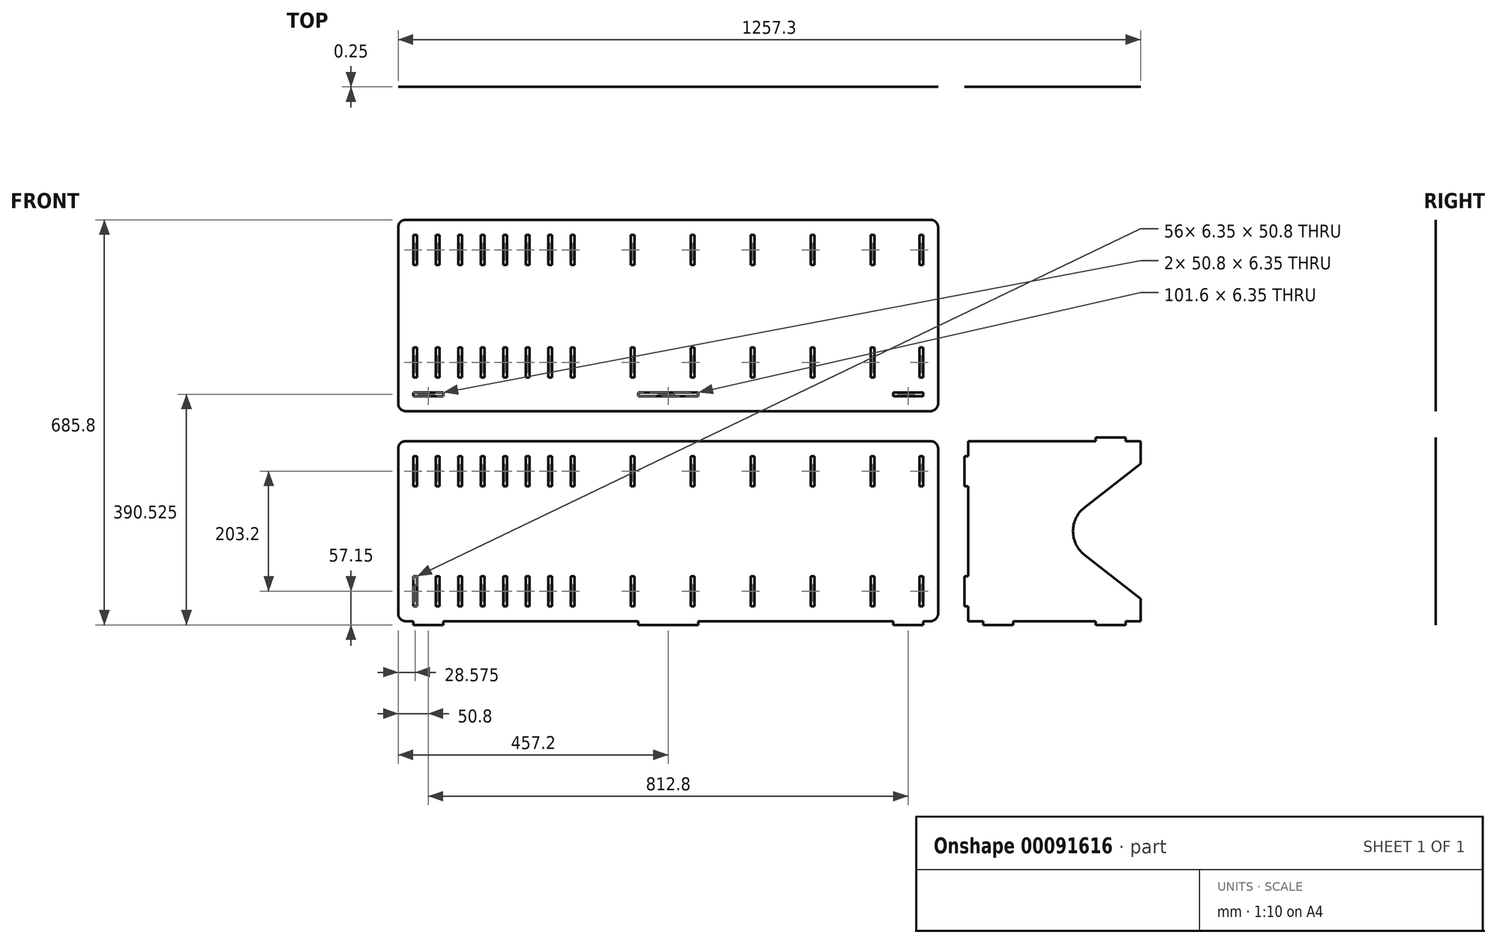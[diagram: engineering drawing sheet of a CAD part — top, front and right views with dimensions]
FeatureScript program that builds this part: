
annotation { "Feature Type Name" : "Feature", "Feature Type Description" : "" }
export const myFeature = defineFeature(function(context is Context, id is Id, definition is map)
    precondition{}
    {
        {
            assignVariable(context, id + "F0", {"name" : "Thickness", "anyValue" : .25});
        }
        {
            var Q0;
            Q0=qCreatedBy(makeId("Front.planeOp"),FACE);
            var sketch = newSketch(context, id + "F1", { "sketchPlane" : qUnion([Q0])});
            skLineSegment(sketch, "E0.bottom", {"start": v(-444.5, 152.4) * mm, "end": v(444.5, 152.4) * mm});
            skLineSegment(sketch, "E0.top", {"start": v(-444.5, -152.4) * mm, "end": v(444.5, -152.4) * mm});
            skLineSegment(sketch, "E0.left", {"start": v(-457.2, 139.7) * mm, "end": v(-457.2, -139.7) * mm});
            skLineSegment(sketch, "E0.right", {"start": v(457.2, 139.7) * mm, "end": v(457.2, -139.7) * mm});
            skPoint(sketch, "E0.middle", {"position": v(0, 0) * mm});
            skLineSegment(sketch, "E1.bottom", {"start": v(-431.8, 152.4) * mm, "end": v(-381, 152.4) * mm});
            skLineSegment(sketch, "E1.top", {"start": v(-431.8, 158.75) * mm, "end": v(-381, 158.75) * mm});
            skLineSegment(sketch, "E1.left", {"start": v(-431.8, 152.4) * mm, "end": v(-431.8, 158.75) * mm});
            skLineSegment(sketch, "E1.right", {"start": v(-381, 152.4) * mm, "end": v(-381, 158.75) * mm});
            skLineSegment(sketch, "E2.bottom", {"start": v(381, 152.4) * mm, "end": v(431.8, 152.4) * mm});
            skLineSegment(sketch, "E2.top", {"start": v(381, 158.75) * mm, "end": v(431.8, 158.75) * mm});
            skLineSegment(sketch, "E2.left", {"start": v(381, 152.4) * mm, "end": v(381, 158.75) * mm});
            skLineSegment(sketch, "E2.right", {"start": v(431.8, 152.4) * mm, "end": v(431.8, 158.75) * mm});
            skLineSegment(sketch, "E3.bottom", {"start": v(-50.8, 152.4) * mm, "end": v(50.8, 152.4) * mm});
            skLineSegment(sketch, "E3.top", {"start": v(-50.8, 158.75) * mm, "end": v(50.8, 158.75) * mm});
            skLineSegment(sketch, "E3.left", {"start": v(-50.8, 152.4) * mm, "end": v(-50.8, 158.75) * mm});
            skLineSegment(sketch, "E3.right", {"start": v(50.8, 152.4) * mm, "end": v(50.8, 158.75) * mm});
            skLineSegment(sketch, "E4", {"start": v(-457.2, 0) * mm, "end": v(457.2, 0) * mm, "construction": true});
            skLineSegment(sketch, "E5.MirrorCS", {"start": v(431.8, -152.4) * mm, "end": v(431.8, -158.75) * mm});
            skLineSegment(sketch, "E6.MirrorCS", {"start": v(381, -152.4) * mm, "end": v(381, -158.75) * mm});
            skLineSegment(sketch, "E7.MirrorCS", {"start": v(-431.8, -152.4) * mm, "end": v(-431.8, -158.75) * mm});
            skLineSegment(sketch, "E8.MirrorCS", {"start": v(-381, -152.4) * mm, "end": v(-381, -158.75) * mm});
            skLineSegment(sketch, "E9.MirrorCS", {"start": v(50.8, -152.4) * mm, "end": v(50.8, -158.75) * mm});
            skLineSegment(sketch, "E10.MirrorCS", {"start": v(-50.8, -152.4) * mm, "end": v(-50.8, -158.75) * mm});
            skLineSegment(sketch, "E11.MirrorCS", {"start": v(-50.8, -152.4) * mm, "end": v(50.8, -152.4) * mm});
            skLineSegment(sketch, "E12.MirrorCS", {"start": v(381, -158.75) * mm, "end": v(431.8, -158.75) * mm});
            skLineSegment(sketch, "E13.MirrorCS", {"start": v(381, -152.4) * mm, "end": v(431.8, -152.4) * mm});
            skLineSegment(sketch, "E14.MirrorCS", {"start": v(-50.8, -158.75) * mm, "end": v(50.8, -158.75) * mm});
            skLineSegment(sketch, "E15.MirrorCS", {"start": v(-431.8, -158.75) * mm, "end": v(-381, -158.75) * mm});
            skLineSegment(sketch, "E16.MirrorCS", {"start": v(-431.8, -152.4) * mm, "end": v(-381, -152.4) * mm});
            skLineSegment(sketch, "E17.bottom", {"start": v(-444.5, 203.2) * mm, "end": v(444.5, 203.2) * mm});
            skLineSegment(sketch, "E17.top", {"start": v(-444.5, 527.05) * mm, "end": v(444.5, 527.05) * mm});
            skLineSegment(sketch, "E17.left", {"start": v(-457.2, 215.9) * mm, "end": v(-457.2, 514.35) * mm});
            skLineSegment(sketch, "E17.right", {"start": v(457.2, 215.9) * mm, "end": v(457.2, 514.35) * mm});
            skLineSegment(sketch, "E18", {"start": v(0, 158.75) * mm, "end": v(0, 228.6) * mm, "construction": true});
            skPoint(sketch, "E18.endSnap0", {"position": v(0, 203.2) * mm});
            skLineSegment(sketch, "E19", {"start": v(0, 193.67) * mm, "end": v(-50.8, 193.67) * mm, "construction": true});
            skPoint(sketch, "E19.endSnap0", {"position": v(0, 193.67) * mm});
            skLineSegment(sketch, "E20.MirrorCS", {"start": v(-50.8, 234.95) * mm, "end": v(-50.8, 228.6) * mm});
            skLineSegment(sketch, "E21.MirrorCS", {"start": v(50.8, 234.95) * mm, "end": v(50.8, 228.6) * mm});
            skLineSegment(sketch, "E22.MirrorCS", {"start": v(431.8, 234.95) * mm, "end": v(431.8, 228.6) * mm});
            skLineSegment(sketch, "E23.MirrorCS", {"start": v(381, 234.95) * mm, "end": v(381, 228.6) * mm});
            skLineSegment(sketch, "E24.MirrorCS", {"start": v(-381, 234.95) * mm, "end": v(-381, 228.6) * mm});
            skLineSegment(sketch, "E25.MirrorCS", {"start": v(-431.8, 234.95) * mm, "end": v(-431.8, 228.6) * mm});
            skLineSegment(sketch, "E26.MirrorCS", {"start": v(-50.8, 228.6) * mm, "end": v(50.8, 228.6) * mm});
            skLineSegment(sketch, "E27.MirrorCS", {"start": v(-50.8, 234.95) * mm, "end": v(50.8, 234.95) * mm});
            skLineSegment(sketch, "E28.MirrorCS", {"start": v(381, 228.6) * mm, "end": v(431.8, 228.6) * mm});
            skLineSegment(sketch, "E29.MirrorCS", {"start": v(381, 234.95) * mm, "end": v(431.8, 234.95) * mm});
            skLineSegment(sketch, "E30.MirrorCS", {"start": v(-431.8, 234.95) * mm, "end": v(-381, 234.95) * mm});
            skLineSegment(sketch, "E31.MirrorCS", {"start": v(-431.8, 228.6) * mm, "end": v(-381, 228.6) * mm});
            skLineSegment(sketch, "E32.bottom", {"start": v(431.8, 127) * mm, "end": v(425.45, 127) * mm});
            skLineSegment(sketch, "E32.top", {"start": v(431.8, 76.2) * mm, "end": v(425.45, 76.2) * mm});
            skLineSegment(sketch, "E32.left", {"start": v(431.8, 127) * mm, "end": v(431.8, 76.2) * mm});
            skLineSegment(sketch, "E32.right", {"start": v(425.45, 127) * mm, "end": v(425.45, 76.2) * mm});
            skLineSegment(sketch, "E33.MirrorCS", {"start": v(431.8, -127) * mm, "end": v(431.8, -76.2) * mm});
            skLineSegment(sketch, "E34.MirrorCS", {"start": v(431.8, -76.2) * mm, "end": v(425.45, -76.2) * mm});
            skLineSegment(sketch, "E35.MirrorCS", {"start": v(431.8, -127) * mm, "end": v(425.45, -127) * mm});
            skLineSegment(sketch, "E36.MirrorCS", {"start": v(425.45, -127) * mm, "end": v(425.45, -76.2) * mm});
            skLineSegment(sketch, "E37", {"start": v(0, 0) * mm, "end": v(0, -152.4) * mm, "construction": true});
            skLineSegment(sketch, "E38.MirrorCS", {"start": v(-431.8, -127) * mm, "end": v(-425.45, -127) * mm});
            skLineSegment(sketch, "E39.MirrorCS", {"start": v(-431.8, 76.2) * mm, "end": v(-425.45, 76.2) * mm});
            skLineSegment(sketch, "E40.MirrorCS", {"start": v(-431.8, -76.2) * mm, "end": v(-425.45, -76.2) * mm});
            skLineSegment(sketch, "E41.MirrorCS", {"start": v(-431.8, 127) * mm, "end": v(-425.45, 127) * mm});
            skLineSegment(sketch, "E42.MirrorCS", {"start": v(-431.8, 127) * mm, "end": v(-431.8, 76.2) * mm});
            skLineSegment(sketch, "E43.MirrorCS", {"start": v(-431.8, -127) * mm, "end": v(-431.8, -76.2) * mm});
            skLineSegment(sketch, "E44.MirrorCS", {"start": v(-425.45, -127) * mm, "end": v(-425.45, -76.2) * mm});
            skLineSegment(sketch, "E45.MirrorCS", {"start": v(-425.45, 127) * mm, "end": v(-425.45, 76.2) * mm});
            skLineSegment(sketch, "E46.bottom", {"start": v(431.8, 260.35) * mm, "end": v(425.45, 260.35) * mm});
            skLineSegment(sketch, "E46.top", {"start": v(431.8, 311.15) * mm, "end": v(425.45, 311.15) * mm});
            skLineSegment(sketch, "E46.left", {"start": v(431.8, 260.35) * mm, "end": v(431.8, 311.15) * mm});
            skLineSegment(sketch, "E46.right", {"start": v(425.45, 260.35) * mm, "end": v(425.45, 311.15) * mm});
            skLineSegment(sketch, "E47.MirrorCS", {"start": v(-431.8, 311.15) * mm, "end": v(-425.45, 311.15) * mm});
            skLineSegment(sketch, "E48.MirrorCS", {"start": v(-431.8, 260.35) * mm, "end": v(-425.45, 260.35) * mm});
            skLineSegment(sketch, "E49.MirrorCS", {"start": v(-431.8, 260.35) * mm, "end": v(-431.8, 311.15) * mm});
            skLineSegment(sketch, "E50.MirrorCS", {"start": v(-425.45, 260.35) * mm, "end": v(-425.45, 311.15) * mm});
            skLineSegment(sketch, "E51.bottom", {"start": v(508, 152.4) * mm, "end": v(800.1, 152.4) * mm});
            skLineSegment(sketch, "E51.top", {"start": v(508, -152.4) * mm, "end": v(800.1, -152.4) * mm});
            skLineSegment(sketch, "E51.left", {"start": v(508, 152.4) * mm, "end": v(508, -152.4) * mm});
            skLineSegment(sketch, "E51.right", {"start": v(800.1, 152.4) * mm, "end": v(800.1, -152.4) * mm});
            skLineSegment(sketch, "E52.bottom", {"start": v(508, 127) * mm, "end": v(501.65, 127) * mm});
            skLineSegment(sketch, "E52.top", {"start": v(508, 76.2) * mm, "end": v(501.65, 76.2) * mm});
            skLineSegment(sketch, "E52.left", {"start": v(508, 127) * mm, "end": v(508, 76.2) * mm});
            skLineSegment(sketch, "E52.right", {"start": v(501.65, 127) * mm, "end": v(501.65, 76.2) * mm});
            skLineSegment(sketch, "E53.bottom", {"start": v(508, -127) * mm, "end": v(501.65, -127) * mm});
            skLineSegment(sketch, "E53.top", {"start": v(508, -76.2) * mm, "end": v(501.65, -76.2) * mm});
            skLineSegment(sketch, "E53.left", {"start": v(508, -127) * mm, "end": v(508, -76.2) * mm});
            skLineSegment(sketch, "E53.right", {"start": v(501.65, -127) * mm, "end": v(501.65, -76.2) * mm});
            skLineSegment(sketch, "E54.bottom", {"start": v(533.4, 152.4) * mm, "end": v(584.2, 152.4) * mm});
            skLineSegment(sketch, "E54.top", {"start": v(533.4, 158.75) * mm, "end": v(584.2, 158.75) * mm});
            skLineSegment(sketch, "E54.left", {"start": v(533.4, 152.4) * mm, "end": v(533.4, 158.75) * mm});
            skLineSegment(sketch, "E54.right", {"start": v(584.2, 152.4) * mm, "end": v(584.2, 158.75) * mm});
            skLineSegment(sketch, "E55", {"start": v(654.05, 152.4) * mm, "end": v(654.05, -152.4) * mm, "construction": true});
            skLineSegment(sketch, "E56.MirrorCS", {"start": v(723.9, 152.4) * mm, "end": v(723.9, 158.75) * mm});
            skLineSegment(sketch, "E57.MirrorCS", {"start": v(774.7, 152.4) * mm, "end": v(774.7, 158.75) * mm});
            skLineSegment(sketch, "E58.MirrorCS", {"start": v(774.7, 152.4) * mm, "end": v(723.9, 152.4) * mm});
            skLineSegment(sketch, "E59.MirrorCS", {"start": v(774.7, 158.75) * mm, "end": v(723.9, 158.75) * mm});
            skLineSegment(sketch, "E60.MirrorCS", {"start": v(723.9, -152.4) * mm, "end": v(723.9, -158.75) * mm});
            skLineSegment(sketch, "E61.MirrorCS", {"start": v(774.7, -152.4) * mm, "end": v(774.7, -158.75) * mm});
            skLineSegment(sketch, "E62.MirrorCS", {"start": v(533.4, -152.4) * mm, "end": v(533.4, -158.75) * mm});
            skLineSegment(sketch, "E63.MirrorCS", {"start": v(584.2, -152.4) * mm, "end": v(584.2, -158.75) * mm});
            skLineSegment(sketch, "E64.MirrorCS", {"start": v(774.7, -152.4) * mm, "end": v(723.9, -152.4) * mm});
            skLineSegment(sketch, "E65.MirrorCS", {"start": v(533.4, -152.4) * mm, "end": v(584.2, -152.4) * mm});
            skLineSegment(sketch, "E66.MirrorCS", {"start": v(533.4, -158.75) * mm, "end": v(584.2, -158.75) * mm});
            skLineSegment(sketch, "E67.MirrorCS", {"start": v(774.7, -158.75) * mm, "end": v(723.9, -158.75) * mm});
            skLineSegment(sketch, "E68", {"start": v(381, 234.95) * mm, "end": v(381, 527.05) * mm, "construction": true});
            skLineSegment(sketch, "E69", {"start": v(381, 381) * mm, "end": v(-457.2, 381) * mm, "construction": true});
            skLineSegment(sketch, "E70.MirrorCS", {"start": v(431.8, 450.85) * mm, "end": v(425.45, 450.85) * mm});
            skLineSegment(sketch, "E71.MirrorCS", {"start": v(431.8, 501.65) * mm, "end": v(425.45, 501.65) * mm});
            skLineSegment(sketch, "E72.MirrorCS", {"start": v(-431.8, 450.85) * mm, "end": v(-425.45, 450.85) * mm});
            skLineSegment(sketch, "E73.MirrorCS", {"start": v(-431.8, 501.65) * mm, "end": v(-425.45, 501.65) * mm});
            skLineSegment(sketch, "E74.MirrorCS", {"start": v(425.45, 501.65) * mm, "end": v(425.45, 450.85) * mm});
            skLineSegment(sketch, "E75.MirrorCS", {"start": v(-425.45, 501.65) * mm, "end": v(-425.45, 450.85) * mm});
            skLineSegment(sketch, "E76.MirrorCS", {"start": v(431.8, 501.65) * mm, "end": v(431.8, 450.85) * mm});
            skLineSegment(sketch, "E77.MirrorCS", {"start": v(-431.8, 501.65) * mm, "end": v(-431.8, 450.85) * mm});
            skLineSegment(sketch, "E78.1.0.0", {"start": v(-387.35, 127) * mm, "end": v(-387.35, 76.2) * mm});
            skLineSegment(sketch, "E78.1.0.1", {"start": v(-393.7, 127) * mm, "end": v(-393.7, 76.2) * mm});
            skLineSegment(sketch, "E78.1.0.2", {"start": v(-387.35, -127) * mm, "end": v(-387.35, -76.2) * mm});
            skLineSegment(sketch, "E78.1.0.3", {"start": v(-393.7, -127) * mm, "end": v(-393.7, -76.2) * mm});
            skLineSegment(sketch, "E78.1.0.5", {"start": v(-393.7, -127) * mm, "end": v(-387.35, -127) * mm});
            skLineSegment(sketch, "E78.1.0.6", {"start": v(-393.7, 127) * mm, "end": v(-387.35, 127) * mm});
            skLineSegment(sketch, "E78.1.0.7", {"start": v(-393.7, -76.2) * mm, "end": v(-387.35, -76.2) * mm});
            skLineSegment(sketch, "E78.1.0.8", {"start": v(-393.7, 76.2) * mm, "end": v(-387.35, 76.2) * mm});
            skLineSegment(sketch, "E78.2.0.0", {"start": v(-349.25, 127) * mm, "end": v(-349.25, 76.2) * mm});
            skLineSegment(sketch, "E78.2.0.1", {"start": v(-355.6, 127) * mm, "end": v(-355.6, 76.2) * mm});
            skLineSegment(sketch, "E78.2.0.2", {"start": v(-349.25, -127) * mm, "end": v(-349.25, -76.2) * mm});
            skLineSegment(sketch, "E78.2.0.3", {"start": v(-355.6, -127) * mm, "end": v(-355.6, -76.2) * mm});
            skLineSegment(sketch, "E78.2.0.5", {"start": v(-355.6, -127) * mm, "end": v(-349.25, -127) * mm});
            skLineSegment(sketch, "E78.2.0.6", {"start": v(-355.6, 127) * mm, "end": v(-349.25, 127) * mm});
            skLineSegment(sketch, "E78.2.0.7", {"start": v(-355.6, -76.2) * mm, "end": v(-349.25, -76.2) * mm});
            skLineSegment(sketch, "E78.2.0.8", {"start": v(-355.6, 76.2) * mm, "end": v(-349.25, 76.2) * mm});
            skLineSegment(sketch, "E78.3.0.0", {"start": v(-311.15, 127) * mm, "end": v(-311.15, 76.2) * mm});
            skLineSegment(sketch, "E78.3.0.1", {"start": v(-317.5, 127) * mm, "end": v(-317.5, 76.2) * mm});
            skLineSegment(sketch, "E78.3.0.2", {"start": v(-311.15, -127) * mm, "end": v(-311.15, -76.2) * mm});
            skLineSegment(sketch, "E78.3.0.3", {"start": v(-317.5, -127) * mm, "end": v(-317.5, -76.2) * mm});
            skLineSegment(sketch, "E78.3.0.5", {"start": v(-317.5, -127) * mm, "end": v(-311.15, -127) * mm});
            skLineSegment(sketch, "E78.3.0.6", {"start": v(-317.5, 127) * mm, "end": v(-311.15, 127) * mm});
            skLineSegment(sketch, "E78.3.0.7", {"start": v(-317.5, -76.2) * mm, "end": v(-311.15, -76.2) * mm});
            skLineSegment(sketch, "E78.3.0.8", {"start": v(-317.5, 76.2) * mm, "end": v(-311.15, 76.2) * mm});
            skLineSegment(sketch, "E78.4.0.0", {"start": v(-273.05, 127) * mm, "end": v(-273.05, 76.2) * mm});
            skLineSegment(sketch, "E78.4.0.1", {"start": v(-279.4, 127) * mm, "end": v(-279.4, 76.2) * mm});
            skLineSegment(sketch, "E78.4.0.2", {"start": v(-273.05, -127) * mm, "end": v(-273.05, -76.2) * mm});
            skLineSegment(sketch, "E78.4.0.3", {"start": v(-279.4, -127) * mm, "end": v(-279.4, -76.2) * mm});
            skLineSegment(sketch, "E78.4.0.5", {"start": v(-279.4, -127) * mm, "end": v(-273.05, -127) * mm});
            skLineSegment(sketch, "E78.4.0.6", {"start": v(-279.4, 127) * mm, "end": v(-273.05, 127) * mm});
            skLineSegment(sketch, "E78.4.0.7", {"start": v(-279.4, -76.2) * mm, "end": v(-273.05, -76.2) * mm});
            skLineSegment(sketch, "E78.4.0.8", {"start": v(-279.4, 76.2) * mm, "end": v(-273.05, 76.2) * mm});
            skLineSegment(sketch, "E78.5.0.0", {"start": v(-234.95, 127) * mm, "end": v(-234.95, 76.2) * mm});
            skLineSegment(sketch, "E78.5.0.1", {"start": v(-241.3, 127) * mm, "end": v(-241.3, 76.2) * mm});
            skLineSegment(sketch, "E78.5.0.2", {"start": v(-234.95, -127) * mm, "end": v(-234.95, -76.2) * mm});
            skLineSegment(sketch, "E78.5.0.3", {"start": v(-241.3, -127) * mm, "end": v(-241.3, -76.2) * mm});
            skLineSegment(sketch, "E78.5.0.5", {"start": v(-241.3, -127) * mm, "end": v(-234.95, -127) * mm});
            skLineSegment(sketch, "E78.5.0.6", {"start": v(-241.3, 127) * mm, "end": v(-234.95, 127) * mm});
            skLineSegment(sketch, "E78.5.0.7", {"start": v(-241.3, -76.2) * mm, "end": v(-234.95, -76.2) * mm});
            skLineSegment(sketch, "E78.5.0.8", {"start": v(-241.3, 76.2) * mm, "end": v(-234.95, 76.2) * mm});
            skLineSegment(sketch, "E78.6.0.0", {"start": v(-196.85, 127) * mm, "end": v(-196.85, 76.2) * mm});
            skLineSegment(sketch, "E78.6.0.1", {"start": v(-203.2, 127) * mm, "end": v(-203.2, 76.2) * mm});
            skLineSegment(sketch, "E78.6.0.2", {"start": v(-196.85, -127) * mm, "end": v(-196.85, -76.2) * mm});
            skLineSegment(sketch, "E78.6.0.3", {"start": v(-203.2, -127) * mm, "end": v(-203.2, -76.2) * mm});
            skLineSegment(sketch, "E78.6.0.5", {"start": v(-203.2, -127) * mm, "end": v(-196.85, -127) * mm});
            skLineSegment(sketch, "E78.6.0.6", {"start": v(-203.2, 127) * mm, "end": v(-196.85, 127) * mm});
            skLineSegment(sketch, "E78.6.0.7", {"start": v(-203.2, -76.2) * mm, "end": v(-196.85, -76.2) * mm});
            skLineSegment(sketch, "E78.6.0.8", {"start": v(-203.2, 76.2) * mm, "end": v(-196.85, 76.2) * mm});
            skLineSegment(sketch, "E78.7.0.0", {"start": v(-158.75, 127) * mm, "end": v(-158.75, 76.2) * mm});
            skLineSegment(sketch, "E78.7.0.1", {"start": v(-165.1, 127) * mm, "end": v(-165.1, 76.2) * mm});
            skLineSegment(sketch, "E78.7.0.2", {"start": v(-158.75, -127) * mm, "end": v(-158.75, -76.2) * mm});
            skLineSegment(sketch, "E78.7.0.3", {"start": v(-165.1, -127) * mm, "end": v(-165.1, -76.2) * mm});
            skLineSegment(sketch, "E78.7.0.5", {"start": v(-165.1, -127) * mm, "end": v(-158.75, -127) * mm});
            skLineSegment(sketch, "E78.7.0.6", {"start": v(-165.1, 127) * mm, "end": v(-158.75, 127) * mm});
            skLineSegment(sketch, "E78.7.0.7", {"start": v(-165.1, -76.2) * mm, "end": v(-158.75, -76.2) * mm});
            skLineSegment(sketch, "E78.7.0.8", {"start": v(-165.1, 76.2) * mm, "end": v(-158.75, 76.2) * mm});
            skLineSegment(sketch, "E78.direction1", {"start": v(-425.45, 76.2) * mm, "end": v(-387.35, 76.2) * mm, "construction": true});
            skLineSegment(sketch, "E79.1.0.0", {"start": v(-63.5, -127) * mm, "end": v(-63.5, -76.2) * mm});
            skLineSegment(sketch, "E79.1.0.1", {"start": v(-57.15, -127) * mm, "end": v(-57.15, -76.2) * mm});
            skLineSegment(sketch, "E79.1.0.2", {"start": v(-63.5, 127) * mm, "end": v(-63.5, 76.2) * mm});
            skLineSegment(sketch, "E79.1.0.3", {"start": v(-57.15, 127) * mm, "end": v(-57.15, 76.2) * mm});
            skLineSegment(sketch, "E79.1.0.4", {"start": v(-63.5, -76.2) * mm, "end": v(-57.15, -76.2) * mm});
            skLineSegment(sketch, "E79.1.0.5", {"start": v(-63.5, 76.2) * mm, "end": v(-57.15, 76.2) * mm});
            skLineSegment(sketch, "E79.1.0.6", {"start": v(-63.5, 127) * mm, "end": v(-57.15, 127) * mm});
            skLineSegment(sketch, "E79.1.0.7", {"start": v(-63.5, -127) * mm, "end": v(-57.15, -127) * mm});
            skLineSegment(sketch, "E79.2.0.0", {"start": v(38.1, -127) * mm, "end": v(38.1, -76.2) * mm});
            skLineSegment(sketch, "E79.2.0.1", {"start": v(44.45, -127) * mm, "end": v(44.45, -76.2) * mm});
            skLineSegment(sketch, "E79.2.0.2", {"start": v(38.1, 127) * mm, "end": v(38.1, 76.2) * mm});
            skLineSegment(sketch, "E79.2.0.3", {"start": v(44.45, 127) * mm, "end": v(44.45, 76.2) * mm});
            skLineSegment(sketch, "E79.2.0.4", {"start": v(38.1, -76.2) * mm, "end": v(44.45, -76.2) * mm});
            skLineSegment(sketch, "E79.2.0.5", {"start": v(38.1, 76.2) * mm, "end": v(44.45, 76.2) * mm});
            skLineSegment(sketch, "E79.2.0.6", {"start": v(38.1, 127) * mm, "end": v(44.45, 127) * mm});
            skLineSegment(sketch, "E79.2.0.7", {"start": v(38.1, -127) * mm, "end": v(44.45, -127) * mm});
            skLineSegment(sketch, "E79.3.0.0", {"start": v(139.7, -127) * mm, "end": v(139.7, -76.2) * mm});
            skLineSegment(sketch, "E79.3.0.1", {"start": v(146.05, -127) * mm, "end": v(146.05, -76.2) * mm});
            skLineSegment(sketch, "E79.3.0.2", {"start": v(139.7, 127) * mm, "end": v(139.7, 76.2) * mm});
            skLineSegment(sketch, "E79.3.0.3", {"start": v(146.05, 127) * mm, "end": v(146.05, 76.2) * mm});
            skLineSegment(sketch, "E79.3.0.4", {"start": v(139.7, -76.2) * mm, "end": v(146.05, -76.2) * mm});
            skLineSegment(sketch, "E79.3.0.5", {"start": v(139.7, 76.2) * mm, "end": v(146.05, 76.2) * mm});
            skLineSegment(sketch, "E79.3.0.6", {"start": v(139.7, 127) * mm, "end": v(146.05, 127) * mm});
            skLineSegment(sketch, "E79.3.0.7", {"start": v(139.7, -127) * mm, "end": v(146.05, -127) * mm});
            skLineSegment(sketch, "E79.4.0.0", {"start": v(241.3, -127) * mm, "end": v(241.3, -76.2) * mm});
            skLineSegment(sketch, "E79.4.0.1", {"start": v(247.65, -127) * mm, "end": v(247.65, -76.2) * mm});
            skLineSegment(sketch, "E79.4.0.2", {"start": v(241.3, 127) * mm, "end": v(241.3, 76.2) * mm});
            skLineSegment(sketch, "E79.4.0.3", {"start": v(247.65, 127) * mm, "end": v(247.65, 76.2) * mm});
            skLineSegment(sketch, "E79.4.0.4", {"start": v(241.3, -76.2) * mm, "end": v(247.65, -76.2) * mm});
            skLineSegment(sketch, "E79.4.0.5", {"start": v(241.3, 76.2) * mm, "end": v(247.65, 76.2) * mm});
            skLineSegment(sketch, "E79.4.0.6", {"start": v(241.3, 127) * mm, "end": v(247.65, 127) * mm});
            skLineSegment(sketch, "E79.4.0.7", {"start": v(241.3, -127) * mm, "end": v(247.65, -127) * mm});
            skLineSegment(sketch, "E79.5.0.0", {"start": v(342.9, -127) * mm, "end": v(342.9, -76.2) * mm});
            skLineSegment(sketch, "E79.5.0.1", {"start": v(349.25, -127) * mm, "end": v(349.25, -76.2) * mm});
            skLineSegment(sketch, "E79.5.0.2", {"start": v(342.9, 127) * mm, "end": v(342.9, 76.2) * mm});
            skLineSegment(sketch, "E79.5.0.3", {"start": v(349.25, 127) * mm, "end": v(349.25, 76.2) * mm});
            skLineSegment(sketch, "E79.5.0.4", {"start": v(342.9, -76.2) * mm, "end": v(349.25, -76.2) * mm});
            skLineSegment(sketch, "E79.5.0.5", {"start": v(342.9, 76.2) * mm, "end": v(349.25, 76.2) * mm});
            skLineSegment(sketch, "E79.5.0.6", {"start": v(342.9, 127) * mm, "end": v(349.25, 127) * mm});
            skLineSegment(sketch, "E79.5.0.7", {"start": v(342.9, -127) * mm, "end": v(349.25, -127) * mm});
            skLineSegment(sketch, "E79.direction1", {"start": v(-165.1, -127) * mm, "end": v(-63.5, -127) * mm, "construction": true});
            skLineSegment(sketch, "E80.1.0.0", {"start": v(-387.35, 501.65) * mm, "end": v(-387.35, 450.85) * mm});
            skLineSegment(sketch, "E80.1.0.1", {"start": v(-387.35, 260.35) * mm, "end": v(-387.35, 311.15) * mm});
            skLineSegment(sketch, "E80.1.0.2", {"start": v(-393.7, 260.35) * mm, "end": v(-393.7, 311.15) * mm});
            skLineSegment(sketch, "E80.1.0.3", {"start": v(-393.7, 501.65) * mm, "end": v(-393.7, 450.85) * mm});
            skLineSegment(sketch, "E80.1.0.4", {"start": v(-393.7, 311.15) * mm, "end": v(-387.35, 311.15) * mm});
            skLineSegment(sketch, "E80.1.0.5", {"start": v(-393.7, 260.35) * mm, "end": v(-387.35, 260.35) * mm});
            skLineSegment(sketch, "E80.1.0.6", {"start": v(-393.7, 501.65) * mm, "end": v(-387.35, 501.65) * mm});
            skLineSegment(sketch, "E80.1.0.7", {"start": v(-393.7, 450.85) * mm, "end": v(-387.35, 450.85) * mm});
            skLineSegment(sketch, "E80.2.0.0", {"start": v(-349.25, 501.65) * mm, "end": v(-349.25, 450.85) * mm});
            skLineSegment(sketch, "E80.2.0.1", {"start": v(-349.25, 260.35) * mm, "end": v(-349.25, 311.15) * mm});
            skLineSegment(sketch, "E80.2.0.2", {"start": v(-355.6, 260.35) * mm, "end": v(-355.6, 311.15) * mm});
            skLineSegment(sketch, "E80.2.0.3", {"start": v(-355.6, 501.65) * mm, "end": v(-355.6, 450.85) * mm});
            skLineSegment(sketch, "E80.2.0.4", {"start": v(-355.6, 311.15) * mm, "end": v(-349.25, 311.15) * mm});
            skLineSegment(sketch, "E80.2.0.5", {"start": v(-355.6, 260.35) * mm, "end": v(-349.25, 260.35) * mm});
            skLineSegment(sketch, "E80.2.0.6", {"start": v(-355.6, 501.65) * mm, "end": v(-349.25, 501.65) * mm});
            skLineSegment(sketch, "E80.2.0.7", {"start": v(-355.6, 450.85) * mm, "end": v(-349.25, 450.85) * mm});
            skLineSegment(sketch, "E80.3.0.0", {"start": v(-311.15, 501.65) * mm, "end": v(-311.15, 450.85) * mm});
            skLineSegment(sketch, "E80.3.0.1", {"start": v(-311.15, 260.35) * mm, "end": v(-311.15, 311.15) * mm});
            skLineSegment(sketch, "E80.3.0.2", {"start": v(-317.5, 260.35) * mm, "end": v(-317.5, 311.15) * mm});
            skLineSegment(sketch, "E80.3.0.3", {"start": v(-317.5, 501.65) * mm, "end": v(-317.5, 450.85) * mm});
            skLineSegment(sketch, "E80.3.0.4", {"start": v(-317.5, 311.15) * mm, "end": v(-311.15, 311.15) * mm});
            skLineSegment(sketch, "E80.3.0.5", {"start": v(-317.5, 260.35) * mm, "end": v(-311.15, 260.35) * mm});
            skLineSegment(sketch, "E80.3.0.6", {"start": v(-317.5, 501.65) * mm, "end": v(-311.15, 501.65) * mm});
            skLineSegment(sketch, "E80.3.0.7", {"start": v(-317.5, 450.85) * mm, "end": v(-311.15, 450.85) * mm});
            skLineSegment(sketch, "E80.4.0.0", {"start": v(-273.05, 501.65) * mm, "end": v(-273.05, 450.85) * mm});
            skLineSegment(sketch, "E80.4.0.1", {"start": v(-273.05, 260.35) * mm, "end": v(-273.05, 311.15) * mm});
            skLineSegment(sketch, "E80.4.0.2", {"start": v(-279.4, 260.35) * mm, "end": v(-279.4, 311.15) * mm});
            skLineSegment(sketch, "E80.4.0.3", {"start": v(-279.4, 501.65) * mm, "end": v(-279.4, 450.85) * mm});
            skLineSegment(sketch, "E80.4.0.4", {"start": v(-279.4, 311.15) * mm, "end": v(-273.05, 311.15) * mm});
            skLineSegment(sketch, "E80.4.0.5", {"start": v(-279.4, 260.35) * mm, "end": v(-273.05, 260.35) * mm});
            skLineSegment(sketch, "E80.4.0.6", {"start": v(-279.4, 501.65) * mm, "end": v(-273.05, 501.65) * mm});
            skLineSegment(sketch, "E80.4.0.7", {"start": v(-279.4, 450.85) * mm, "end": v(-273.05, 450.85) * mm});
            skLineSegment(sketch, "E80.5.0.0", {"start": v(-234.95, 501.65) * mm, "end": v(-234.95, 450.85) * mm});
            skLineSegment(sketch, "E80.5.0.1", {"start": v(-234.95, 260.35) * mm, "end": v(-234.95, 311.15) * mm});
            skLineSegment(sketch, "E80.5.0.2", {"start": v(-241.3, 260.35) * mm, "end": v(-241.3, 311.15) * mm});
            skLineSegment(sketch, "E80.5.0.3", {"start": v(-241.3, 501.65) * mm, "end": v(-241.3, 450.85) * mm});
            skLineSegment(sketch, "E80.5.0.4", {"start": v(-241.3, 311.15) * mm, "end": v(-234.95, 311.15) * mm});
            skLineSegment(sketch, "E80.5.0.5", {"start": v(-241.3, 260.35) * mm, "end": v(-234.95, 260.35) * mm});
            skLineSegment(sketch, "E80.5.0.6", {"start": v(-241.3, 501.65) * mm, "end": v(-234.95, 501.65) * mm});
            skLineSegment(sketch, "E80.5.0.7", {"start": v(-241.3, 450.85) * mm, "end": v(-234.95, 450.85) * mm});
            skLineSegment(sketch, "E80.6.0.0", {"start": v(-196.85, 501.65) * mm, "end": v(-196.85, 450.85) * mm});
            skLineSegment(sketch, "E80.6.0.1", {"start": v(-196.85, 260.35) * mm, "end": v(-196.85, 311.15) * mm});
            skLineSegment(sketch, "E80.6.0.2", {"start": v(-203.2, 260.35) * mm, "end": v(-203.2, 311.15) * mm});
            skLineSegment(sketch, "E80.6.0.3", {"start": v(-203.2, 501.65) * mm, "end": v(-203.2, 450.85) * mm});
            skLineSegment(sketch, "E80.6.0.4", {"start": v(-203.2, 311.15) * mm, "end": v(-196.85, 311.15) * mm});
            skLineSegment(sketch, "E80.6.0.5", {"start": v(-203.2, 260.35) * mm, "end": v(-196.85, 260.35) * mm});
            skLineSegment(sketch, "E80.6.0.6", {"start": v(-203.2, 501.65) * mm, "end": v(-196.85, 501.65) * mm});
            skLineSegment(sketch, "E80.6.0.7", {"start": v(-203.2, 450.85) * mm, "end": v(-196.85, 450.85) * mm});
            skLineSegment(sketch, "E80.7.0.0", {"start": v(-158.75, 501.65) * mm, "end": v(-158.75, 450.85) * mm});
            skLineSegment(sketch, "E80.7.0.1", {"start": v(-158.75, 260.35) * mm, "end": v(-158.75, 311.15) * mm});
            skLineSegment(sketch, "E80.7.0.2", {"start": v(-165.1, 260.35) * mm, "end": v(-165.1, 311.15) * mm});
            skLineSegment(sketch, "E80.7.0.3", {"start": v(-165.1, 501.65) * mm, "end": v(-165.1, 450.85) * mm});
            skLineSegment(sketch, "E80.7.0.4", {"start": v(-165.1, 311.15) * mm, "end": v(-158.75, 311.15) * mm});
            skLineSegment(sketch, "E80.7.0.5", {"start": v(-165.1, 260.35) * mm, "end": v(-158.75, 260.35) * mm});
            skLineSegment(sketch, "E80.7.0.6", {"start": v(-165.1, 501.65) * mm, "end": v(-158.75, 501.65) * mm});
            skLineSegment(sketch, "E80.7.0.7", {"start": v(-165.1, 450.85) * mm, "end": v(-158.75, 450.85) * mm});
            skLineSegment(sketch, "E80.direction1", {"start": v(-425.45, 450.85) * mm, "end": v(-387.35, 450.85) * mm, "construction": true});
            skLineSegment(sketch, "E81.1.0.0", {"start": v(-63.5, 501.65) * mm, "end": v(-63.5, 450.85) * mm});
            skLineSegment(sketch, "E81.1.0.1", {"start": v(-57.15, 260.35) * mm, "end": v(-57.15, 311.15) * mm});
            skLineSegment(sketch, "E81.1.0.2", {"start": v(-63.5, 260.35) * mm, "end": v(-63.5, 311.15) * mm});
            skLineSegment(sketch, "E81.1.0.3", {"start": v(-57.15, 501.65) * mm, "end": v(-57.15, 450.85) * mm});
            skLineSegment(sketch, "E81.1.0.4", {"start": v(-63.5, 311.15) * mm, "end": v(-57.15, 311.15) * mm});
            skLineSegment(sketch, "E81.1.0.5", {"start": v(-63.5, 501.65) * mm, "end": v(-57.15, 501.65) * mm});
            skLineSegment(sketch, "E81.1.0.6", {"start": v(-63.5, 450.85) * mm, "end": v(-57.15, 450.85) * mm});
            skLineSegment(sketch, "E81.1.0.7", {"start": v(-63.5, 260.35) * mm, "end": v(-57.15, 260.35) * mm});
            skLineSegment(sketch, "E81.2.0.0", {"start": v(38.1, 501.65) * mm, "end": v(38.1, 450.85) * mm});
            skLineSegment(sketch, "E81.2.0.1", {"start": v(44.45, 260.35) * mm, "end": v(44.45, 311.15) * mm});
            skLineSegment(sketch, "E81.2.0.2", {"start": v(38.1, 260.35) * mm, "end": v(38.1, 311.15) * mm});
            skLineSegment(sketch, "E81.2.0.3", {"start": v(44.45, 501.65) * mm, "end": v(44.45, 450.85) * mm});
            skLineSegment(sketch, "E81.2.0.4", {"start": v(38.1, 311.15) * mm, "end": v(44.45, 311.15) * mm});
            skLineSegment(sketch, "E81.2.0.5", {"start": v(38.1, 501.65) * mm, "end": v(44.45, 501.65) * mm});
            skLineSegment(sketch, "E81.2.0.6", {"start": v(38.1, 450.85) * mm, "end": v(44.45, 450.85) * mm});
            skLineSegment(sketch, "E81.2.0.7", {"start": v(38.1, 260.35) * mm, "end": v(44.45, 260.35) * mm});
            skLineSegment(sketch, "E81.3.0.0", {"start": v(139.7, 501.65) * mm, "end": v(139.7, 450.85) * mm});
            skLineSegment(sketch, "E81.3.0.1", {"start": v(146.05, 260.35) * mm, "end": v(146.05, 311.15) * mm});
            skLineSegment(sketch, "E81.3.0.2", {"start": v(139.7, 260.35) * mm, "end": v(139.7, 311.15) * mm});
            skLineSegment(sketch, "E81.3.0.3", {"start": v(146.05, 501.65) * mm, "end": v(146.05, 450.85) * mm});
            skLineSegment(sketch, "E81.3.0.4", {"start": v(139.7, 311.15) * mm, "end": v(146.05, 311.15) * mm});
            skLineSegment(sketch, "E81.3.0.5", {"start": v(139.7, 501.65) * mm, "end": v(146.05, 501.65) * mm});
            skLineSegment(sketch, "E81.3.0.6", {"start": v(139.7, 450.85) * mm, "end": v(146.05, 450.85) * mm});
            skLineSegment(sketch, "E81.3.0.7", {"start": v(139.7, 260.35) * mm, "end": v(146.05, 260.35) * mm});
            skLineSegment(sketch, "E81.4.0.0", {"start": v(241.3, 501.65) * mm, "end": v(241.3, 450.85) * mm});
            skLineSegment(sketch, "E81.4.0.1", {"start": v(247.65, 260.35) * mm, "end": v(247.65, 311.15) * mm});
            skLineSegment(sketch, "E81.4.0.2", {"start": v(241.3, 260.35) * mm, "end": v(241.3, 311.15) * mm});
            skLineSegment(sketch, "E81.4.0.3", {"start": v(247.65, 501.65) * mm, "end": v(247.65, 450.85) * mm});
            skLineSegment(sketch, "E81.4.0.4", {"start": v(241.3, 311.15) * mm, "end": v(247.65, 311.15) * mm});
            skLineSegment(sketch, "E81.4.0.5", {"start": v(241.3, 501.65) * mm, "end": v(247.65, 501.65) * mm});
            skLineSegment(sketch, "E81.4.0.6", {"start": v(241.3, 450.85) * mm, "end": v(247.65, 450.85) * mm});
            skLineSegment(sketch, "E81.4.0.7", {"start": v(241.3, 260.35) * mm, "end": v(247.65, 260.35) * mm});
            skLineSegment(sketch, "E81.5.0.0", {"start": v(342.9, 501.65) * mm, "end": v(342.9, 450.85) * mm});
            skLineSegment(sketch, "E81.5.0.1", {"start": v(349.25, 260.35) * mm, "end": v(349.25, 311.15) * mm});
            skLineSegment(sketch, "E81.5.0.2", {"start": v(342.9, 260.35) * mm, "end": v(342.9, 311.15) * mm});
            skLineSegment(sketch, "E81.5.0.3", {"start": v(349.25, 501.65) * mm, "end": v(349.25, 450.85) * mm});
            skLineSegment(sketch, "E81.5.0.4", {"start": v(342.9, 311.15) * mm, "end": v(349.25, 311.15) * mm});
            skLineSegment(sketch, "E81.5.0.5", {"start": v(342.9, 501.65) * mm, "end": v(349.25, 501.65) * mm});
            skLineSegment(sketch, "E81.5.0.6", {"start": v(342.9, 450.85) * mm, "end": v(349.25, 450.85) * mm});
            skLineSegment(sketch, "E81.5.0.7", {"start": v(342.9, 260.35) * mm, "end": v(349.25, 260.35) * mm});
            skLineSegment(sketch, "E81.direction1", {"start": v(-165.1, 450.85) * mm, "end": v(-63.5, 450.85) * mm, "construction": true});
            skPoint(sketch, "E82.visualSharp", {"position": v(-457.2, 527.05) * mm});
            skArc(sketch, "E82.filletArc", {"start": v(-444.5, 527.05) * mm, "mid": v(-453.48, 523.33) * mm, "end": v(-457.2, 514.35) * mm});
            skPoint(sketch, "E83.visualSharp", {"position": v(457.2, 527.05) * mm});
            skArc(sketch, "E83.filletArc", {"start": v(457.2, 514.35) * mm, "mid": v(453.48, 523.33) * mm, "end": v(444.5, 527.05) * mm});
            skPoint(sketch, "E84.visualSharp", {"position": v(457.2, 203.2) * mm});
            skArc(sketch, "E84.filletArc", {"start": v(444.5, 203.2) * mm, "mid": v(453.48, 206.92) * mm, "end": v(457.2, 215.9) * mm});
            skPoint(sketch, "E85.visualSharp", {"position": v(-457.2, 203.2) * mm});
            skArc(sketch, "E85.filletArc", {"start": v(-457.2, 215.9) * mm, "mid": v(-453.48, 206.92) * mm, "end": v(-444.5, 203.2) * mm});
            skPoint(sketch, "E86.visualSharp", {"position": v(-457.2, 152.4) * mm});
            skArc(sketch, "E86.filletArc", {"start": v(-444.5, 152.4) * mm, "mid": v(-453.48, 148.68) * mm, "end": v(-457.2, 139.7) * mm});
            skPoint(sketch, "E87.visualSharp", {"position": v(457.2, 152.4) * mm});
            skArc(sketch, "E87.filletArc", {"start": v(457.2, 139.7) * mm, "mid": v(453.48, 148.68) * mm, "end": v(444.5, 152.4) * mm});
            skPoint(sketch, "E88.visualSharp", {"position": v(457.2, -152.4) * mm});
            skArc(sketch, "E88.filletArc", {"start": v(444.5, -152.4) * mm, "mid": v(453.48, -148.68) * mm, "end": v(457.2, -139.7) * mm});
            skPoint(sketch, "E89.visualSharp", {"position": v(-457.2, -152.4) * mm});
            skArc(sketch, "E89.filletArc", {"start": v(-457.2, -139.7) * mm, "mid": v(-453.48, -148.68) * mm, "end": v(-444.5, -152.4) * mm});
            skLineSegment(sketch, "E90", {"start": v(705.17, 40) * mm, "end": v(800.1, 114.3) * mm});
            skLineSegment(sketch, "E91", {"start": v(705.17, -40) * mm, "end": v(800.1, -114.3) * mm});
            skPoint(sketch, "E92.visualSharp", {"position": v(654.05, 0) * mm});
            skArc(sketch, "E92.filletArc", {"start": v(705.17, 40) * mm, "mid": v(685.68, 0) * mm, "end": v(705.17, -40) * mm});
            skSolve(sketch);
        }
        {
            var Q0;
            Q0=makeQuery(id+"F1.imprint","IMPRINT",FACE,{"disambiguationData":[TD([[makeQuery(id+"F1.imprint","IMPRINT",EDGE,{"derivedFrom":sQuery(id+"F1.wireOp",EDGE,"E17.bottom")}),1.0]])]});
            var Q1;
            {var subQ8=sQuery(id+"F1.wireOp",EDGE,"E0.left");Q1=makeQuery(id+"F1.imprint","IMPRINT",FACE,{"disambiguationData":[TD([[makeQuery(id+"F1.imprint","IMPRINT",EDGE,{"derivedFrom":subQ8}),1.0]])]});}
            var Q2;
            Q2=makeQuery(id+"F1.imprint","IMPRINT",FACE,{"disambiguationData":[TD([[makeQuery(id+"F1.imprint","IMPRINT",EDGE,{"derivedFrom":sQuery(id+"F1.wireOp",EDGE,"E1.bottom")}),1.0]])]});
            var Q3;
            Q3=makeQuery(id+"F1.imprint","IMPRINT",FACE,{"disambiguationData":[TD([[makeQuery(id+"F1.imprint","IMPRINT",EDGE,{"derivedFrom":sQuery(id+"F1.wireOp",EDGE,"E3.bottom")}),1.0]])]});
            var Q4;
            Q4=makeQuery(id+"F1.imprint","IMPRINT",FACE,{"disambiguationData":[TD([[makeQuery(id+"F1.imprint","IMPRINT",EDGE,{"derivedFrom":sQuery(id+"F1.wireOp",EDGE,"E2.bottom")}),1.0]])]});
            var Q5;
            Q5=makeQuery(id+"F1.imprint","IMPRINT",FACE,{"disambiguationData":[TD([[makeQuery(id+"F1.imprint","IMPRINT",EDGE,{"derivedFrom":sQuery(id+"F1.wireOp",EDGE,"E54.bottom")}),1.0]])]});
            var Q6;
            Q6=makeQuery(id+"F1.imprint","IMPRINT",FACE,{"disambiguationData":[TD([[makeQuery(id+"F1.imprint","IMPRINT",EDGE,{"derivedFrom":sQuery(id+"F1.wireOp",EDGE,"E56.MirrorCS")}),-1.0]])]});
            var Q7;
            Q7=makeQuery(id+"F1.imprint","IMPRINT",FACE,{"disambiguationData":[TD([[makeQuery(id+"F1.imprint","IMPRINT",EDGE,{"derivedFrom":sQuery(id+"F1.wireOp",EDGE,"E52.bottom")}),1.0]])]});
            var Q8;
            Q8=makeQuery(id+"F1.imprint","IMPRINT",FACE,{"disambiguationData":[TD([[makeQuery(id+"F1.imprint","IMPRINT",EDGE,{"derivedFrom":sQuery(id+"F1.wireOp",EDGE,"E53.bottom")}),-1.0]])]});
            var Q9;
            {var subQ4=sQuery(id+"F1.wireOp",EDGE,"E51.top");Q9=makeQuery(id+"F1.imprint","IMPRINT",FACE,{"disambiguationData":[TD([[makeQuery(id+"F1.imprint","IMPRINT",EDGE,{"derivedFrom":subQ4}),1.0]])]});}
            var Q10;
            Q10=makeQuery(id+"F1.imprint","IMPRINT",FACE,{"disambiguationData":[TD([[makeQuery(id+"F1.imprint","IMPRINT",EDGE,{"derivedFrom":sQuery(id+"F1.wireOp",EDGE,"E5.MirrorCS")}),-1.0]])]});
            var Q11;
            Q11=makeQuery(id+"F1.imprint","IMPRINT",FACE,{"disambiguationData":[TD([[makeQuery(id+"F1.imprint","IMPRINT",EDGE,{"derivedFrom":sQuery(id+"F1.wireOp",EDGE,"E9.MirrorCS")}),-1.0]])]});
            var Q12;
            Q12=makeQuery(id+"F1.imprint","IMPRINT",FACE,{"disambiguationData":[TD([[makeQuery(id+"F1.imprint","IMPRINT",EDGE,{"derivedFrom":sQuery(id+"F1.wireOp",EDGE,"E7.MirrorCS")}),1.0]])]});
            var Q13;
            Q13=makeQuery(id+"F1.imprint","IMPRINT",FACE,{"disambiguationData":[TD([[makeQuery(id+"F1.imprint","IMPRINT",EDGE,{"derivedFrom":sQuery(id+"F1.wireOp",EDGE,"E60.MirrorCS")}),1.0]])]});
            var Q14;
            Q14=makeQuery(id+"F1.imprint","IMPRINT",FACE,{"disambiguationData":[TD([[makeQuery(id+"F1.imprint","IMPRINT",EDGE,{"derivedFrom":sQuery(id+"F1.wireOp",EDGE,"E62.MirrorCS")}),1.0]])]});
            extrude(context, id + "F2", {"entities" : qUnion([Q0, Q1, Q2, Q3, Q4, Q5, Q6, Q7, Q8, Q9, Q10, Q11, Q12, Q13, Q14]), "depth" : (getVariable(context, 'Thickness')) * mm});
        }
    });
